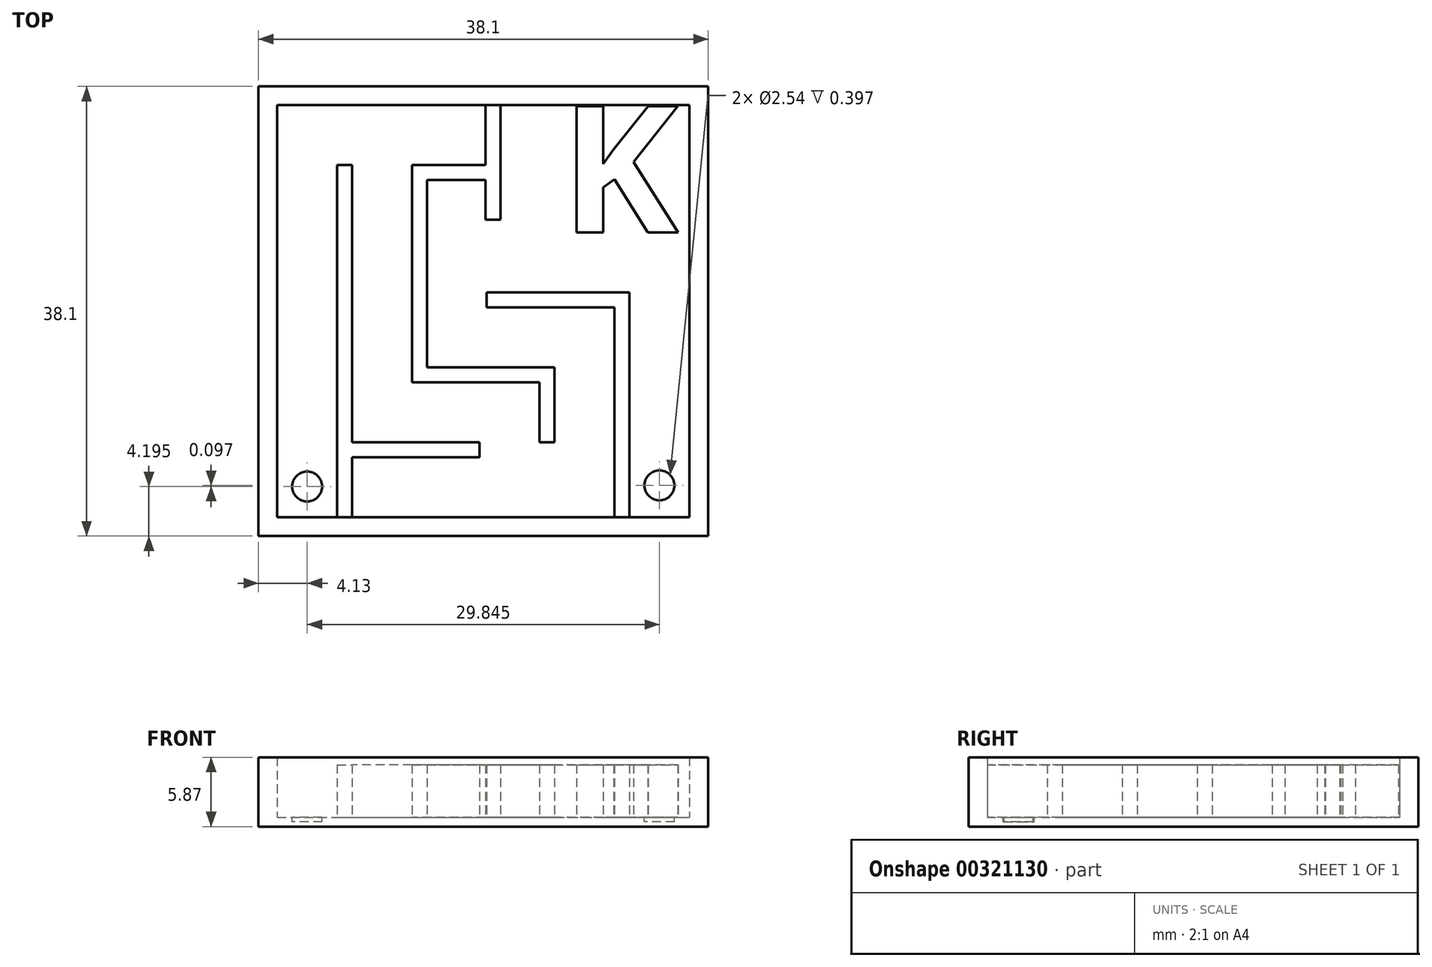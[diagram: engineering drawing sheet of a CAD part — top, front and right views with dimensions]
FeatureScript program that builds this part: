
annotation { "Feature Type Name" : "Feature", "Feature Type Description" : "" }
export const myFeature = defineFeature(function(context is Context, id is Id, definition is map)
    precondition{}
    {
        {
            var Q0;
            Q0=qCreatedBy(makeId("Top.planeOp"),FACE);
            var sketch = newSketch(context, id + "F0", { "sketchPlane" : qUnion([Q0])});
            skLineSegment(sketch, "E0.bottom", {"start": v(-19.54, 18.52) * mm, "end": v(18.56, 18.52) * mm});
            skLineSegment(sketch, "E0.top", {"start": v(-19.54, -19.58) * mm, "end": v(18.56, -19.58) * mm});
            skLineSegment(sketch, "E0.left", {"start": v(-19.54, 18.52) * mm, "end": v(-19.54, -19.58) * mm});
            skLineSegment(sketch, "E0.right", {"start": v(18.56, 18.52) * mm, "end": v(18.56, -19.58) * mm});
            skSolve(sketch);
        }
        {
            var Q0;
            Q0 = qSketchRegion(id + "F0", true);
            extrude(context, id + "F1", {"entities" : qUnion([Q0]), "depth" : 0.8 * mm});
        }
        {
            var Q0;
            Q0=makeQuery(id+"F1.opExtrude","CAP_FACE",FACE,{"disambiguationData":[OSD([sQuery(id+"F0.wireOp",EDGE,"E0.bottom"),sQuery(id+"F0.wireOp",EDGE,"E0.top"),sQuery(id+"F0.wireOp",EDGE,"E0.left"),sQuery(id+"F0.wireOp",EDGE,"E0.right")])],"isStart":false});
            var sketch = newSketch(context, id + "F2", { "sketchPlane" : qUnion([Q0])});
            skLineSegment(sketch, "E1.0", {"start": v(-17.95, 16.93) * mm, "end": v(16.97, 16.93) * mm});
            skLineSegment(sketch, "E1.1", {"start": v(-17.95, 16.93) * mm, "end": v(-17.95, -18) * mm});
            skLineSegment(sketch, "E1.2", {"start": v(-17.95, -18) * mm, "end": v(16.97, -18) * mm});
            skLineSegment(sketch, "E1.3", {"start": v(16.97, 16.93) * mm, "end": v(16.97, -18) * mm});
            skSolve(sketch);
        }
        {
            var Q0;
            Q0=makeQuery(id+"F2.imprint","IMPRINT",FACE,{"disambiguationData":[TD([[makeQuery(id+"F2.imprint","IMPRINT",EDGE,{"derivedFrom":sQuery(id+"F2.wireOp",EDGE,"E1.0")}),1.0]])]});
            extrude(context, id + "F3", {"entities" : qUnion([Q0]), "operationType" : NewBodyOperationType.ADD, "depth" : 5.08 * mm});
        }
        {
            var Q0;
            Q0=makeQuery(id+"F1.opExtrude","CAP_FACE",FACE,{"disambiguationData":[OSD([sQuery(id+"F0.wireOp",EDGE,"E0.bottom"),sQuery(id+"F0.wireOp",EDGE,"E0.top"),sQuery(id+"F0.wireOp",EDGE,"E0.left"),sQuery(id+"F0.wireOp",EDGE,"E0.right")])],"isStart":false});
            var sketch = newSketch(context, id + "F4", { "sketchPlane" : qUnion([Q0])});
            skLineSegment(sketch, "E2.bottom", {"start": v(-12.87, -18) * mm, "end": v(-11.6, -18) * mm});
            skLineSegment(sketch, "E2.top", {"start": v(-12.87, 11.85) * mm, "end": v(-11.6, 11.85) * mm});
            skLineSegment(sketch, "E2.left", {"start": v(-12.87, -18) * mm, "end": v(-12.87, 11.85) * mm});
            skLineSegment(sketch, "E2.right", {"start": v(-11.6, -18) * mm, "end": v(-11.6, -12.92) * mm});
            skLineSegment(sketch, "E3", {"start": v(-6.52, 11.85) * mm, "end": v(-0.3, 11.85) * mm});
            skLineSegment(sketch, "E4", {"start": v(-0.3, 11.85) * mm, "end": v(-0.3, 16.93) * mm});
            skLineSegment(sketch, "E5", {"start": v(-6.52, 11.85) * mm, "end": v(-6.52, 10.58) * mm});
            skLineSegment(sketch, "E6", {"start": v(0.97, 7.23) * mm, "end": v(0.97, 16.93) * mm});
            skLineSegment(sketch, "E7", {"start": v(-0.3, 16.93) * mm, "end": v(0.97, 16.93) * mm});
            skLineSegment(sketch, "E8", {"start": v(5.54, -11.65) * mm, "end": v(4.27, -11.65) * mm});
            skLineSegment(sketch, "E9", {"start": v(4.27, -11.65) * mm, "end": v(4.27, -6.57) * mm});
            skLineSegment(sketch, "E10", {"start": v(4.27, -6.57) * mm, "end": v(-6.52, -6.57) * mm});
            skLineSegment(sketch, "E11", {"start": v(-6.52, -6.57) * mm, "end": v(-6.52, 5.5) * mm});
            skLineSegment(sketch, "E12", {"start": v(-6.52, 5.5) * mm, "end": v(-6.52, 5.5) * mm});
            skLineSegment(sketch, "E13", {"start": v(-11.6, -11.65) * mm, "end": v(-0.8, -11.65) * mm});
            skLineSegment(sketch, "E14", {"start": v(-0.8, -11.65) * mm, "end": v(-0.8, -12.92) * mm});
            skLineSegment(sketch, "E15", {"start": v(-0.8, -12.92) * mm, "end": v(-11.6, -12.92) * mm});
            skLineSegment(sketch, "E16", {"start": v(11.9, -18) * mm, "end": v(11.9, 1.05) * mm});
            skLineSegment(sketch, "E17", {"start": v(11.9, 1.05) * mm, "end": v(-0.22, 1.05) * mm});
            skLineSegment(sketch, "E18", {"start": v(-0.22, 1.05) * mm, "end": v(-0.22, -0.22) * mm});
            skLineSegment(sketch, "E19", {"start": v(-0.22, -0.22) * mm, "end": v(10.62, -0.22) * mm});
            skLineSegment(sketch, "E20", {"start": v(10.62, -0.22) * mm, "end": v(10.62, -18) * mm});
            skPoint(sketch, "E21.start.orphan", {"position": v(1.1, -5.3) * mm});
            skLineSegment(sketch, "E22", {"start": v(-6.52, 5.5) * mm, "end": v(-6.52, 10.58) * mm});
            skLineSegment(sketch, "E23.trimOffspring", {"start": v(-11.6, -11.65) * mm, "end": v(-11.6, 11.85) * mm});
            skLineSegment(sketch, "E24", {"start": v(-5.25, -5.3) * mm, "end": v(5.54, -5.3) * mm});
            skLineSegment(sketch, "E25", {"start": v(5.54, -5.3) * mm, "end": v(5.54, -11.65) * mm});
            skLineSegment(sketch, "E26.left", {"start": v(16.97, 5.5) * mm, "end": v(16.97, 6.13) * mm});
            skLineSegment(sketch, "E27", {"start": v(-17.95, -18) * mm, "end": v(-12.87, -18) * mm});
            skPoint(sketch, "E28.centerSnap0", {"position": v(-15.41, -18) * mm});
            skLineSegment(sketch, "E29", {"start": v(11.9, -18) * mm, "end": v(16.97, -18) * mm});
            skPoint(sketch, "E30.centerSnap0", {"position": v(14.43, -18) * mm});
            skLineSegment(sketch, "E31", {"start": v(-0.3, 7.23) * mm, "end": v(0.97, 7.23) * mm});
            skLineSegment(sketch, "E32", {"start": v(-0.3, 7.23) * mm, "end": v(-0.3, 10.58) * mm});
            skLineSegment(sketch, "E33", {"start": v(-0.3, 10.58) * mm, "end": v(-5.25, 10.58) * mm});
            skLineSegment(sketch, "E34", {"start": v(-5.25, 10.58) * mm, "end": v(-5.25, -5.3) * mm});
            skText(sketch, "E35", { "text": "K", "fontName": "OpenSans-Bold.ttf"});
            const initialGuessF4  = {"E35": [0.00605, 0.00613, 1, 0, 0.0108]};
            skSetInitialGuess(sketch, initialGuessF4);
            skSolve(sketch);
        }
        {
            var Q0;
            Q0 = qSketchRegion(id + "F4", true);
            var Q1;
            {var subQ0=sQuery(id+"F4.wireOp",EDGE,"E16");Q1=makeQuery(id+"F4.imprint","IMPRINT",FACE,{"disambiguationData":[TD([[makeQuery(id+"F4.imprint","IMPRINT",EDGE,{"derivedFrom":subQ0}),1.0]])]});}
            extrude(context, id + "F5", {"entities" : qUnion([Q0, Q1]), "operationType" : NewBodyOperationType.ADD, "depth" : 4.44 * mm});
        }
        {
            var Q0;
            Q0=makeQuery(id+"F1.opExtrude","CAP_FACE",FACE,{"disambiguationData":[OSD([sQuery(id+"F0.wireOp",EDGE,"E0.bottom"),sQuery(id+"F0.wireOp",EDGE,"E0.top"),sQuery(id+"F0.wireOp",EDGE,"E0.left"),sQuery(id+"F0.wireOp",EDGE,"E0.right")])],"isStart":false});
            var sketch = newSketch(context, id + "F6", { "sketchPlane" : qUnion([Q0])});
            skLineSegment(sketch, "E36", {"start": v(-12.87, -18) * mm, "end": v(-17.95, -18) * mm});
            skCircle(sketch, "E37", {"center": v(-15.41, -15.39) * mm, "radius": 1.27 * mm});
            skPoint(sketch, "E37.centerSnap0", {"position": v(-15.41, -18) * mm});
            skLineSegment(sketch, "E38", {"start": v(11.9, -18) * mm, "end": v(16.97, -18) * mm});
            skCircle(sketch, "E39", {"center": v(14.43, -15.29) * mm, "radius": 1.27 * mm});
            skPoint(sketch, "E39.centerSnap0", {"position": v(14.43, -18) * mm});
            skSolve(sketch);
        }
        {
            var Q0;
            Q0 = qSketchRegion(id + "F6", true);
            extrude(context, id + "F7", {"entities" : qUnion([Q0]), "operationType" : NewBodyOperationType.REMOVE, "oppositeDirection" : true, "depth" : 0.4 * mm});
        }
    });
